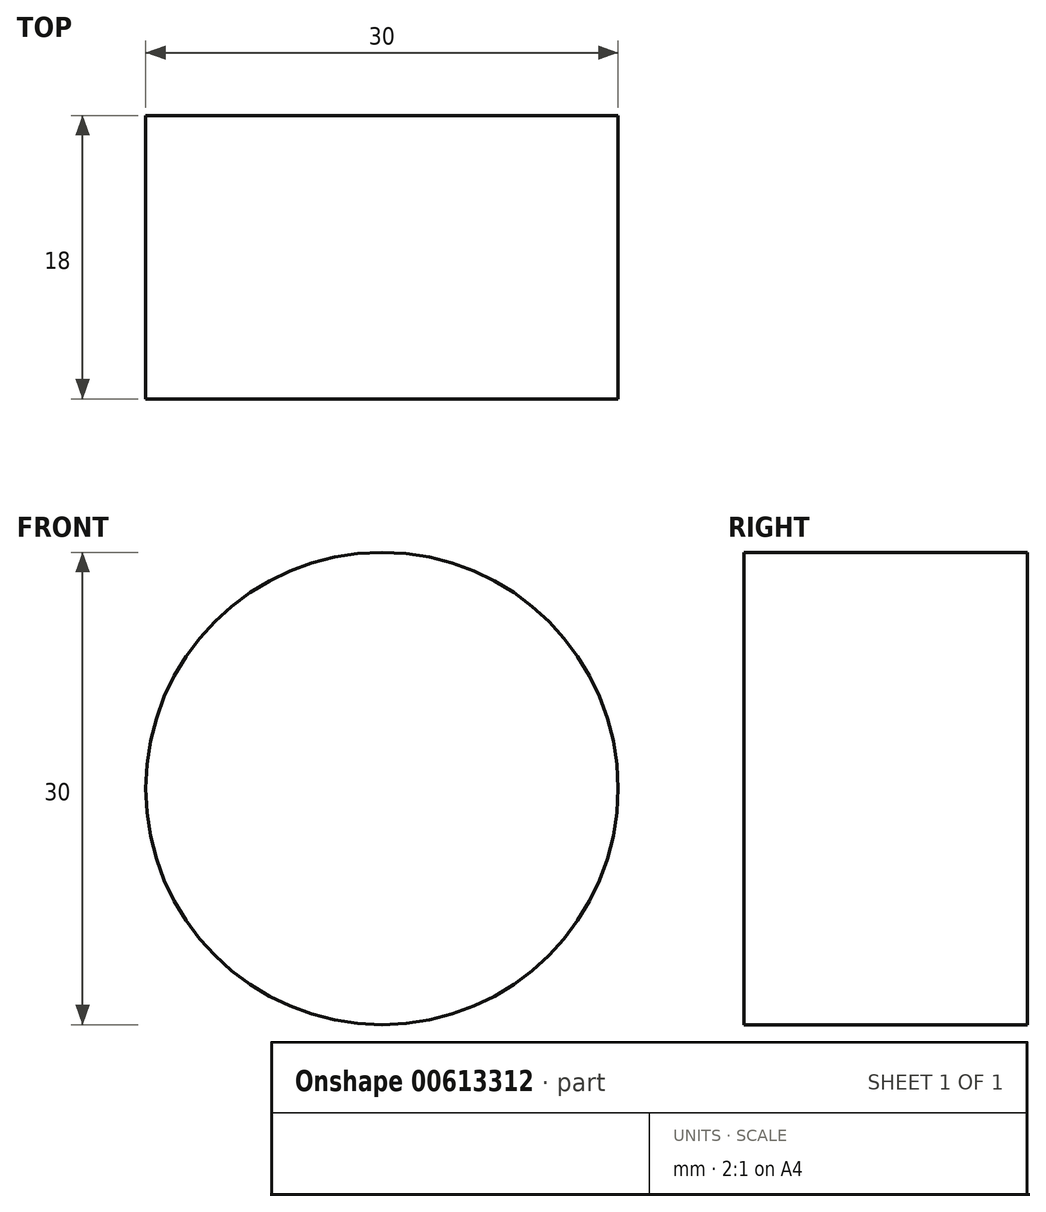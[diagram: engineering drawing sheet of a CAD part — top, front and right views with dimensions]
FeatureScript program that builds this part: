
annotation { "Feature Type Name" : "Feature", "Feature Type Description" : "" }
export const myFeature = defineFeature(function(context is Context, id is Id, definition is map)
    precondition{}
    {
        {
            var Q0;
            Q0=qCreatedBy(makeId("Top.planeOp"),FACE);
            var sketch = newSketch(context, id + "F0", { "sketchPlane" : qUnion([Q0])});
            skCircle(sketch, "E0", {"center": v(0, 0) * mm, "radius": 5 * mm});
            skSolve(sketch);
        }
        {
            var Q0;
            Q0 = qSketchRegion(id + "F0", true);
            extrude(context, id + "F1", {"entities" : qUnion([Q0]), "depth" : 5 * mm, "offsetDistance" : 25 * mm});
        }
        {
            var Q0;
            Q0=qCreatedBy(makeId("Front.planeOp"),FACE);
            var sketch = newSketch(context, id + "F2", { "sketchPlane" : qUnion([Q0])});
            skCircle(sketch, "E1", {"center": v(0, 0) * mm, "radius": 15 * mm});
            skSolve(sketch);
        }
        {
            var Q0;
            Q0=makeQuery(id+"F2.imprint","IMPRINT",FACE,{"disambiguationData":[TD([[makeQuery(id+"F2.imprint","IMPRINT",EDGE,{"derivedFrom":sQuery(id+"F2.wireOp",EDGE,"E1")}),1.0]])]});
            extrude(context, id + "F3", {"entities" : qUnion([Q0]), "operationType" : NewBodyOperationType.ADD, "endBound" : BoundingType.SYMMETRIC, "depth" : 18 * mm, "offsetDistance" : 25 * mm});
        }
    });
